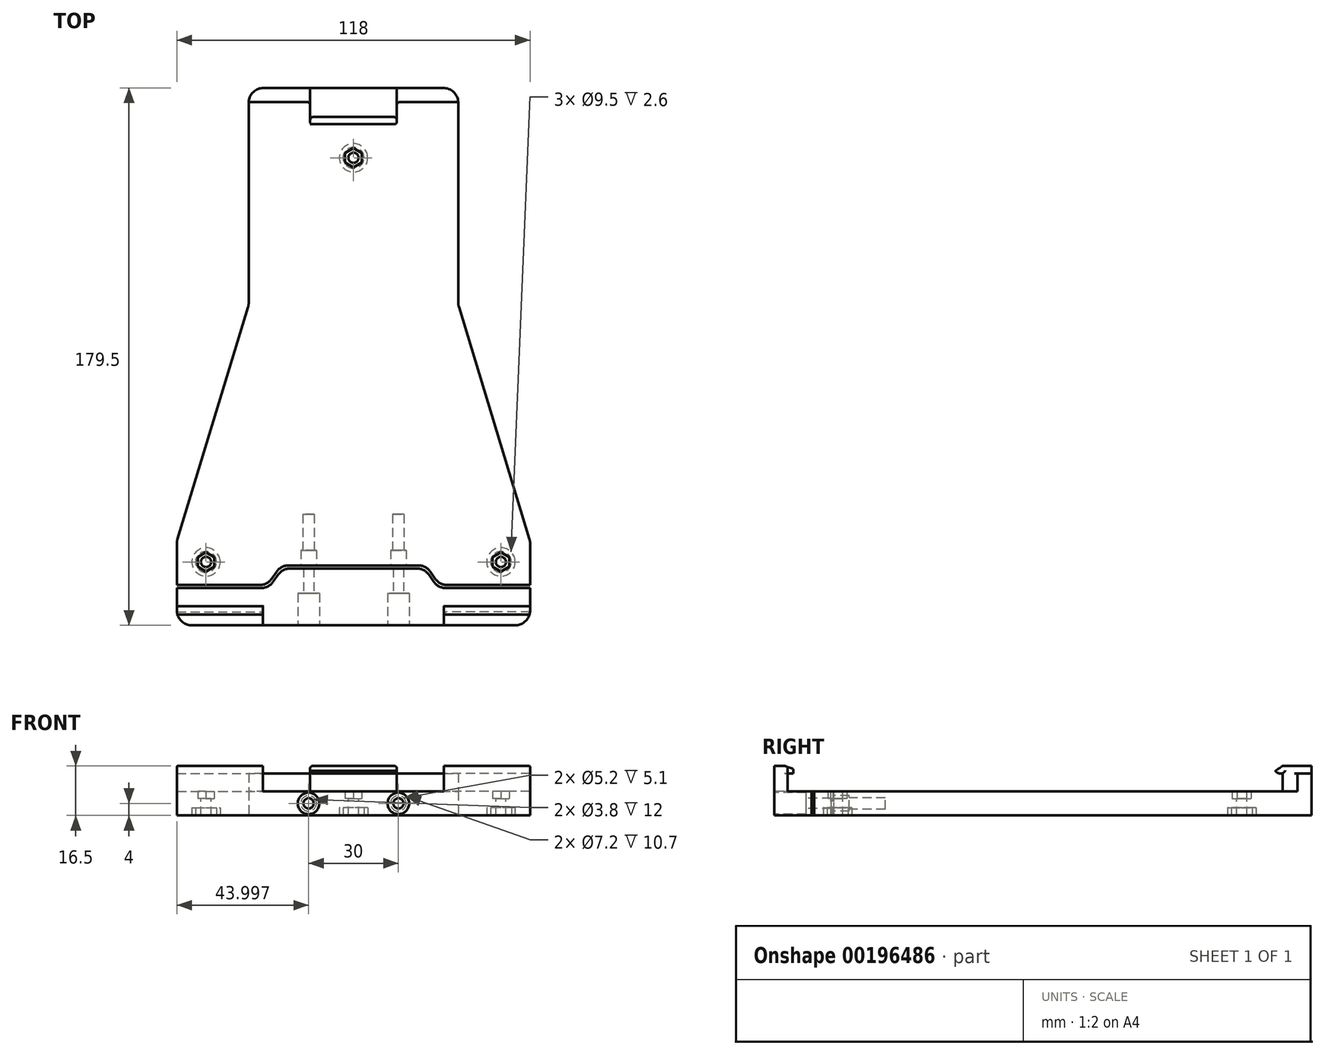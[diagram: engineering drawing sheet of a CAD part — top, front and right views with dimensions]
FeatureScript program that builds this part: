
annotation { "Feature Type Name" : "Feature", "Feature Type Description" : "" }
export const myFeature = defineFeature(function(context is Context, id is Id, definition is map)
    precondition{}
    {
        {
            var Q0;
            Q0=qCreatedBy(makeId("Top.planeOp"),FACE);
            var sketch = newSketch(context, id + "F0", { "sketchPlane" : qUnion([Q0])});
            skLineSegment(sketch, "E0.bottom", {"start": v(47.34, 124.09) * mm, "end": v(17.34, 124.09) * mm});
            skLineSegment(sketch, "E0.top", {"start": v(47.34, 51.59) * mm, "end": v(12.34, 51.59) * mm});
            skLineSegment(sketch, "E0.left", {"start": v(47.34, 124.09) * mm, "end": v(47.34, 51.59) * mm});
            skLineSegment(sketch, "E0.right", {"start": v(12.34, 119.09) * mm, "end": v(12.34, 52.33) * mm});
            skLineSegment(sketch, "E1.bottom", {"start": v(47.34, -27.41) * mm, "end": v(-11.66, -27.41) * mm});
            skLineSegment(sketch, "E1.top", {"start": v(47.34, -55.41) * mm, "end": v(-6.66, -55.41) * mm});
            skLineSegment(sketch, "E1.left", {"start": v(47.34, -27.41) * mm, "end": v(47.34, -55.41) * mm});
            skLineSegment(sketch, "E1.right", {"start": v(-11.66, -28.15) * mm, "end": v(-11.66, -50.41) * mm});
            skLineSegment(sketch, "E2", {"start": v(-11.45, -26.7) * mm, "end": v(12.12, 50.88) * mm});
            skLineSegment(sketch, "E3", {"start": v(47.34, -27.41) * mm, "end": v(47.34, 51.59) * mm});
            skCircle(sketch, "E4", {"center": v(-1.91, -34.26) * mm, "radius": 1.7 * mm});
            skCircle(sketch, "E5", {"center": v(47.34, 100.74) * mm, "radius": 1.7 * mm});
            skCircle(sketch, "E6.cCircle", {"center": v(-1.91, -34.26) * mm, "radius": 3.2 * mm, "construction": true});
            skLineSegment(sketch, "E6.0", {"start": v(-1.91, -37.46) * mm, "end": v(-4.68, -35.86) * mm});
            skLineSegment(sketch, "E6.1", {"start": v(-4.68, -35.86) * mm, "end": v(-4.68, -32.66) * mm});
            skLineSegment(sketch, "E6.2", {"start": v(-4.68, -32.66) * mm, "end": v(-1.91, -31.06) * mm});
            skLineSegment(sketch, "E6.3", {"start": v(-1.91, -31.06) * mm, "end": v(0.86, -32.66) * mm});
            skLineSegment(sketch, "E6.4", {"start": v(0.86, -32.66) * mm, "end": v(0.86, -35.86) * mm});
            skLineSegment(sketch, "E6.5", {"start": v(0.86, -35.86) * mm, "end": v(-1.91, -37.46) * mm});
            skCircle(sketch, "E7.cCircle", {"center": v(47.34, 100.74) * mm, "radius": 3.2 * mm, "construction": true});
            skLineSegment(sketch, "E7.0", {"start": v(47.34, 97.54) * mm, "end": v(44.57, 99.14) * mm});
            skLineSegment(sketch, "E7.1", {"start": v(44.57, 99.14) * mm, "end": v(44.57, 102.34) * mm});
            skLineSegment(sketch, "E7.2", {"start": v(44.57, 102.34) * mm, "end": v(47.34, 103.94) * mm});
            skLineSegment(sketch, "E7.3", {"start": v(47.34, 103.94) * mm, "end": v(50.1, 102.34) * mm});
            skLineSegment(sketch, "E7.4", {"start": v(50.1, 102.34) * mm, "end": v(50.1, 99.14) * mm});
            skLineSegment(sketch, "E7.5", {"start": v(50.1, 99.14) * mm, "end": v(47.34, 97.54) * mm});
            skPoint(sketch, "E8.visualSharp", {"position": v(-11.66, -55.41) * mm});
            skArc(sketch, "E8.filletArc", {"start": v(-11.66, -50.41) * mm, "mid": v(-10.2, -53.95) * mm, "end": v(-6.66, -55.41) * mm});
            skPoint(sketch, "E9.visualSharp", {"position": v(-11.66, -27.41) * mm});
            skArc(sketch, "E9.filletArc", {"start": v(-11.45, -26.7) * mm, "mid": v(-11.6, -27.42) * mm, "end": v(-11.66, -28.15) * mm});
            skPoint(sketch, "E10.visualSharp", {"position": v(12.34, 51.59) * mm});
            skArc(sketch, "E10.filletArc", {"start": v(12.12, 50.88) * mm, "mid": v(12.28, 51.6) * mm, "end": v(12.34, 52.33) * mm});
            skPoint(sketch, "E11.visualSharp", {"position": v(12.34, 124.09) * mm});
            skArc(sketch, "E11.filletArc", {"start": v(17.34, 124.09) * mm, "mid": v(13.8, 122.62) * mm, "end": v(12.34, 119.09) * mm});
            skLineSegment(sketch, "E12", {"start": v(0.86, -35.86) * mm, "end": v(1.25, -34.73) * mm});
            skLineSegment(sketch, "E13.MirrorCS", {"start": v(50.49, 101.3) * mm, "end": v(50.1, 102.34) * mm});
            skPoint(sketch, "E14.end.orphan", {"position": v(47.34, -37.46) * mm});
            skPoint(sketch, "E15.orphan", {"position": v(47.34, -31.06) * mm});
            skLineSegment(sketch, "E16.trimOffspring", {"start": v(44.19, 101.3) * mm, "end": v(44.57, 102.34) * mm});
            skPoint(sketch, "E17.MirrorCS.start.orphan", {"position": v(96.59, -37.46) * mm});
            skPoint(sketch, "E18.orphan", {"position": v(99.36, -32.66) * mm});
            skPoint(sketch, "E19.trimOffspring.end.orphan", {"position": v(47.34, 97.54) * mm});
            skPoint(sketch, "E20.MirrorCS.end.orphan", {"position": v(99.36, -35.86) * mm});
            skPoint(sketch, "E21.trimOffspring.start.orphan", {"position": v(93.82, -35.86) * mm});
            skPoint(sketch, "E22.MirrorCS.start.orphan", {"position": v(96.59, -31.06) * mm});
            skSolve(sketch);
        }
        {
            var Q0;
            Q0=makeQuery(id+"F0.imprint","IMPRINT",FACE,{"disambiguationData":[TD([[makeQuery(id+"F0.imprint","IMPRINT",EDGE,{"derivedFrom":sQuery(id+"F0.wireOp",EDGE,"E1.top")}),-1.0]])]});
            var Q1;
            {var subQ6=sQuery(id+"F0.wireOp",EDGE,"E0.bottom");Q1=makeQuery(id+"F0.imprint","IMPRINT",FACE,{"disambiguationData":[TD([[makeQuery(id+"F0.imprint","IMPRINT",EDGE,{"derivedFrom":subQ6}),1.0]])]});}
            extrude(context, id + "F1", {"entities" : qUnion([Q0, Q1]), "depth" : 2.4 * mm});
        }
        {
            var Q0;
            Q0=makeQuery(id+"F0.imprint","IMPRINT",FACE,{"disambiguationData":[TD([[makeQuery(id+"F0.imprint","IMPRINT",EDGE,{"derivedFrom":sQuery(id+"F0.wireOp",EDGE,"E4")}),-1.0]])]});
            var Q1;
            Q1=makeQuery(id+"F0.imprint","IMPRINT",FACE,{"disambiguationData":[TD([[makeQuery(id+"F0.imprint","IMPRINT",EDGE,{"derivedFrom":sQuery(id+"F0.wireOp",EDGE,"E1.top")}),-1.0]])]});
            var Q2;
            {var subQ4=sQuery(id+"F0.wireOp",EDGE,"E7.0");Q2=makeQuery(id+"F0.imprint","IMPRINT",FACE,{"disambiguationData":[TD([[makeQuery(id+"F0.imprint","IMPRINT",EDGE,{"derivedFrom":subQ4}),-1.0]])]});}
            var Q3;
            {var subQ6=sQuery(id+"F0.wireOp",EDGE,"E0.bottom");Q3=makeQuery(id+"F0.imprint","IMPRINT",FACE,{"disambiguationData":[TD([[makeQuery(id+"F0.imprint","IMPRINT",EDGE,{"derivedFrom":subQ6}),1.0]])]});}
            extrude(context, id + "F2", {"entities" : qUnion([Q0, Q1, Q2, Q3]), "operationType" : NewBodyOperationType.ADD, "oppositeDirection" : true, "depth" : 5.6 * mm});
        }
        {
            var Q0;
            Q0=makeQuery(id+"F2.opExtrude","CAP_FACE",FACE,{"disambiguationData":[OSD([sQuery(id+"F0.wireOp",EDGE,"E0.bottom"),sQuery(id+"F0.wireOp",EDGE,"E0.left"),sQuery(id+"F0.wireOp",EDGE,"E0.right"),sQuery(id+"F0.wireOp",EDGE,"E1.top"),sQuery(id+"F0.wireOp",EDGE,"E1.left"),sQuery(id+"F0.wireOp",EDGE,"E1.right"),sQuery(id+"F0.wireOp",EDGE,"E2"),sQuery(id+"F0.wireOp",EDGE,"E3"),sQuery(id+"F0.wireOp",EDGE,"E4"),sQuery(id+"F0.wireOp",EDGE,"E5"),sQuery(id+"F0.wireOp",EDGE,"E8.filletArc"),sQuery(id+"F0.wireOp",EDGE,"E9.filletArc"),sQuery(id+"F0.wireOp",EDGE,"E10.filletArc"),sQuery(id+"F0.wireOp",EDGE,"E11.filletArc")])],"isStart":false});
            var sketch = newSketch(context, id + "F3", { "sketchPlane" : qUnion([Q0])});
            skCircle(sketch, "E23", {"center": v(-1.91, 34.26) * mm, "radius": 3.5 * mm});
            skCircle(sketch, "E24", {"center": v(47.34, -100.74) * mm, "radius": 3.5 * mm});
            skCircle(sketch, "E25", {"center": v(-1.91, 34.26) * mm, "radius": 4.75 * mm});
            skCircle(sketch, "E26", {"center": v(47.34, -100.74) * mm, "radius": 4.75 * mm});
            skSolve(sketch);
        }
        {
            var Q0;
            {var subQ1=sQuery(id+"F0.wireOp",EDGE,"E0.left");var subQ2=makeQuery(id+"F2.opExtrude","CAP_EDGE",EDGE,{"disambiguationData":[OSD([subQ1])],"isStart":false});var subQ6=sQuery(id+"F3.wireOp",EDGE,"E26");var subQ7=makeQuery(id+"F3.imprint","INTERSECT",VERTEX,{"derivedFrom":[subQ2,subQ6]});Q0=makeQuery(id+"F3.imprint","IMPRINT",FACE,{"disambiguationData":[TD([[makeQuery(id+"F3.imprint","IMPRINT",EDGE,{"disambiguationData":[TD([[subQ7,-1.0]])],"derivedFrom":subQ2}),-1.0]])]});}
            var Q1;
            {var subQ1=sQuery(id+"F0.wireOp",EDGE,"E0.left");var subQ2=makeQuery(id+"F2.opExtrude","CAP_EDGE",EDGE,{"disambiguationData":[OSD([subQ1])],"isStart":false});var subQ6=sQuery(id+"F3.wireOp",EDGE,"E26");var subQ7=makeQuery(id+"F3.imprint","INTERSECT",VERTEX,{"derivedFrom":[subQ2,subQ6]});Q1=makeQuery(id+"F3.imprint","IMPRINT",FACE,{"disambiguationData":[TD([[makeQuery(id+"F3.imprint","IMPRINT",EDGE,{"disambiguationData":[TD([[subQ7,-1.0]])],"derivedFrom":subQ2}),1.0]])]});}
            var Q2;
            Q2=makeQuery(id+"F3.imprint","IMPRINT",FACE,{"disambiguationData":[TD([[makeQuery(id+"F3.imprint","IMPRINT",EDGE,{"derivedFrom":sQuery(id+"F3.wireOp",EDGE,"E23")}),-1.0]])]});
            extrude(context, id + "F4", {"entities" : qUnion([Q0, Q1, Q2]), "operationType" : NewBodyOperationType.REMOVE, "oppositeDirection" : true, "depth" : 2.6 * mm});
        }
        {
            var Q0;
            Q0=makeQuery(id+"F1.opExtrude","CAP_FACE",FACE,{"disambiguationData":[OSD([sQuery(id+"F0.wireOp",EDGE,"E0.bottom"),sQuery(id+"F0.wireOp",EDGE,"E0.left"),sQuery(id+"F0.wireOp",EDGE,"E0.right"),sQuery(id+"F0.wireOp",EDGE,"E1.top"),sQuery(id+"F0.wireOp",EDGE,"E1.left"),sQuery(id+"F0.wireOp",EDGE,"E1.right"),sQuery(id+"F0.wireOp",EDGE,"E2"),sQuery(id+"F0.wireOp",EDGE,"E3"),sQuery(id+"F0.wireOp",EDGE,"E6.0"),sQuery(id+"F0.wireOp",EDGE,"E6.1"),sQuery(id+"F0.wireOp",EDGE,"E6.2"),sQuery(id+"F0.wireOp",EDGE,"E6.3"),sQuery(id+"F0.wireOp",EDGE,"E6.4"),sQuery(id+"F0.wireOp",EDGE,"E6.5"),sQuery(id+"F0.wireOp",EDGE,"E7.0"),sQuery(id+"F0.wireOp",EDGE,"E7.1"),sQuery(id+"F0.wireOp",EDGE,"E7.2"),sQuery(id+"F0.wireOp",EDGE,"E8.filletArc"),sQuery(id+"F0.wireOp",EDGE,"E9.filletArc"),sQuery(id+"F0.wireOp",EDGE,"E10.filletArc"),sQuery(id+"F0.wireOp",EDGE,"E11.filletArc")])],"isStart":false});
            var sketch = newSketch(context, id + "F5", { "sketchPlane" : qUnion([Q0])});
            skLineSegment(sketch, "E27", {"start": v(-11.66, -50.98) * mm, "end": v(16.14, -50.98) * mm});
            skLineSegment(sketch, "E28", {"start": v(47.34, 114.37) * mm, "end": v(33.84, 114.37) * mm});
            skLineSegment(sketch, "E29", {"start": v(17.14, -51.98) * mm, "end": v(17.14, -55.41) * mm});
            skLineSegment(sketch, "E30", {"start": v(32.84, 115.37) * mm, "end": v(32.84, 118.37) * mm});
            skLineSegment(sketch, "E31", {"start": v(31.84, 119.37) * mm, "end": v(12.34, 119.37) * mm});
            skArc(sketch, "E32.filletArc", {"start": v(32.84, 118.37) * mm, "mid": v(32.54, 119.07) * mm, "end": v(31.84, 119.37) * mm});
            skArc(sketch, "E33.filletArc", {"start": v(32.84, 115.37) * mm, "mid": v(33.13, 114.66) * mm, "end": v(33.84, 114.37) * mm});
            skArc(sketch, "E34.filletArc", {"start": v(17.14, -51.98) * mm, "mid": v(16.84, -51.28) * mm, "end": v(16.14, -50.98) * mm});
            skSolve(sketch);
        }
        {
            var Q0;
            {var subQ3=sQuery(id+"F5.wireOp",EDGE,"E29");Q0=makeQuery(id+"F5.imprint","IMPRINT",FACE,{"disambiguationData":[TD([[makeQuery(id+"F5.imprint","IMPRINT",EDGE,{"derivedFrom":subQ3}),-1.0]])]});}
            var Q1;
            {var subQ6=sQuery(id+"F5.wireOp",EDGE,"E28");Q1=makeQuery(id+"F5.imprint","IMPRINT",FACE,{"disambiguationData":[TD([[makeQuery(id+"F5.imprint","IMPRINT",EDGE,{"derivedFrom":subQ6}),-1.0]])]});}
            extrude(context, id + "F6", {"entities" : qUnion([Q0, Q1]), "operationType" : NewBodyOperationType.ADD, "depth" : 6 * mm});
        }
        {
            var Q0;
            {var subQ0=sQuery(id+"F0.wireOp",EDGE,"E0.left");Q0=makeQuery(id+"F6.boolean.opBoolean","MERGE",FACE,{"derivedFrom":[makeQuery(id+"F2.boolean.opBoolean","MERGE",FACE,{"derivedFrom":[makeQuery(id+"F1.opExtrude","SWEPT_FACE",FACE,{"disambiguationData":[OSD([subQ0])]}),makeQuery(id+"F2.opExtrude","SWEPT_FACE",FACE,{"disambiguationData":[OSD([subQ0])]})]}),makeQuery(id+"F6.opExtrude","SWEPT_FACE",FACE,{"disambiguationData":[OSD([subQ0])]})]});}
            var sketch = newSketch(context, id + "F7", { "sketchPlane" : qUnion([Q0])});
            skLineSegment(sketch, "E35", {"start": v(114.37, 8.4) * mm, "end": v(113.61, 8.4) * mm});
            skLineSegment(sketch, "E36", {"start": v(110.77, 8.4) * mm, "end": v(114.37, 10.9) * mm});
            skLineSegment(sketch, "E37.bottom", {"start": v(114.37, 10.9) * mm, "end": v(124.09, 10.9) * mm});
            skLineSegment(sketch, "E37.top", {"start": v(114.37, 8.4) * mm, "end": v(124.09, 8.4) * mm});
            skLineSegment(sketch, "E37.left", {"start": v(114.37, 10.9) * mm, "end": v(114.37, 8.4) * mm});
            skLineSegment(sketch, "E37.right", {"start": v(124.09, 10.9) * mm, "end": v(124.09, 8.4) * mm});
            skLineSegment(sketch, "E38", {"start": v(111.98, 9.24) * mm, "end": v(111.97, 9.26) * mm});
            skPoint(sketch, "E39.newPointA", {"position": v(112.57, 8.4) * mm});
            skPoint(sketch, "E39.newPointB", {"position": v(110.77, 8.4) * mm});
            skArc(sketch, "E39.filletArc", {"start": v(111.97, 9.26) * mm, "mid": v(112.69, 8.63) * mm, "end": v(113.61, 8.4) * mm});
            skSolve(sketch);
        }
        {
            var Q0;
            Q0 = qSketchRegion(id + "F7", true);
            extrude(context, id + "F8", {"entities" : qUnion([Q0]), "operationType" : NewBodyOperationType.ADD, "oppositeDirection" : true, "depth" : 14.5 * mm});
        }
        {
            var Q0;
            {var subQ2=sQuery(id+"F0.wireOp",EDGE,"E0.bottom");var subQ4=sQuery(id+"F7.wireOp",EDGE,"E37.top");var subQ5=sQuery(id+"F7.wireOp",EDGE,"E35");Q0=makeQuery(id+"F8.boolean.opBoolean","SPLIT",EDGE,{"disambiguationData":[TD([makeQuery(id+"F1.opExtrude","SWEPT_FACE",FACE,{"disambiguationData":[OSD([subQ2])]})])],"derivedFrom":makeQuery(id+"F8.opExtrude","CAP_EDGE",EDGE,{"disambiguationData":[OSD([subQ5,subQ4])],"isStart":false})});}
            var Q1;
            Q1=makeQuery(id+"F8.opExtrude","CAP_EDGE",EDGE,{"disambiguationData":[OSD([sQuery(id+"F7.wireOp",EDGE,"E37.bottom")])],"isStart":false});
            fillet(context, id + "F9", {"entities" : qUnion([Q0, Q1]), "radius" : 1 * mm, "tangentPropagation" : true, "rho" : 0.5, "crossSection" : FilletCrossSection.CONIC, "allowEdgeOverflow" : false});
        }
        {
            var Q0;
            Q0=makeQuery(id+"F6.opExtrude","SWEPT_FACE",FACE,{"disambiguationData":[OSD([sQuery(id+"F5.wireOp",EDGE,"E29")])]});
            var sketch = newSketch(context, id + "F10", { "sketchPlane" : qUnion([Q0])});
            skLineSegment(sketch, "E40", {"start": v(-55.41, 8.4) * mm, "end": v(-49.01, 8.4) * mm});
            skLineSegment(sketch, "E41", {"start": v(-55.41, 8.4) * mm, "end": v(-55.41, 10.9) * mm});
            skLineSegment(sketch, "E42", {"start": v(-55.41, 10.9) * mm, "end": v(-51.81, 10.9) * mm});
            skLineSegment(sketch, "E43", {"start": v(-55.41, 8.4) * mm, "end": v(-51.81, 8.4) * mm});
            skLineSegment(sketch, "E44", {"start": v(-49.01, 8.4) * mm, "end": v(-49.01, 9.55) * mm});
            skLineSegment(sketch, "E45", {"start": v(-49.34, 10.02) * mm, "end": v(-51.81, 10.9) * mm});
            skPoint(sketch, "E46.start.orphan", {"position": v(-50.41, 9.65) * mm});
            skPoint(sketch, "E47.visualSharp", {"position": v(-49.01, 9.9) * mm});
            skArc(sketch, "E47.filletArc", {"start": v(-49.01, 9.55) * mm, "mid": v(-49.1, 9.84) * mm, "end": v(-49.34, 10.02) * mm});
            skSolve(sketch);
        }
        {
            var Q0;
            {var subQ0=sQuery(id+"F10.wireOp",EDGE,"E41");Q0=makeQuery(id+"F10.imprint","IMPRINT",FACE,{"disambiguationData":[TD([[makeQuery(id+"F10.imprint","IMPRINT",EDGE,{"derivedFrom":subQ0}),-1.0]])]});}
            extrude(context, id + "F11", {"entities" : qUnion([Q0]), "operationType" : NewBodyOperationType.ADD, "oppositeDirection" : true, "depth" : 28.77 * mm});
        }
        {
            var Q0;
            {var subQ1=sQuery(id+"F0.wireOp",EDGE,"E1.top");var subQ3=sQuery(id+"F10.wireOp",EDGE,"E40");Q0=makeQuery(id+"F11.boolean.opBoolean","SPLIT",FACE,{"disambiguationData":[TD([makeQuery(id+"F1.opExtrude","SWEPT_FACE",FACE,{"disambiguationData":[OSD([subQ1])]})])],"derivedFrom":makeQuery(id+"F11.opExtrude","SWEPT_FACE",FACE,{"disambiguationData":[OSD([subQ3])]})});}
            extrude(context, id + "F12", {"entities" : qUnion([Q0]), "operationType" : NewBodyOperationType.REMOVE, "endBound" : BoundingType.UP_TO_NEXT, "oppositeDirection" : true, "depth" : 25 * mm});
        }
        {
            var Q0;
            Q0=makeQuery(id+"F1.opExtrude","CAP_FACE",FACE,{"disambiguationData":[OSD([sQuery(id+"F0.wireOp",EDGE,"E0.bottom"),sQuery(id+"F0.wireOp",EDGE,"E0.left"),sQuery(id+"F0.wireOp",EDGE,"E0.right"),sQuery(id+"F0.wireOp",EDGE,"E1.top"),sQuery(id+"F0.wireOp",EDGE,"E1.left"),sQuery(id+"F0.wireOp",EDGE,"E1.right"),sQuery(id+"F0.wireOp",EDGE,"E2"),sQuery(id+"F0.wireOp",EDGE,"E3"),sQuery(id+"F0.wireOp",EDGE,"E6.0"),sQuery(id+"F0.wireOp",EDGE,"E6.1"),sQuery(id+"F0.wireOp",EDGE,"E6.2"),sQuery(id+"F0.wireOp",EDGE,"E6.3"),sQuery(id+"F0.wireOp",EDGE,"E6.4"),sQuery(id+"F0.wireOp",EDGE,"E6.5"),sQuery(id+"F0.wireOp",EDGE,"E7.0"),sQuery(id+"F0.wireOp",EDGE,"E7.1"),sQuery(id+"F0.wireOp",EDGE,"E7.2"),sQuery(id+"F0.wireOp",EDGE,"E8.filletArc"),sQuery(id+"F0.wireOp",EDGE,"E9.filletArc"),sQuery(id+"F0.wireOp",EDGE,"E10.filletArc"),sQuery(id+"F0.wireOp",EDGE,"E11.filletArc")])],"isStart":false});
            var sketch = newSketch(context, id + "F13", { "sketchPlane" : qUnion([Q0])});
            skLineSegment(sketch, "E48", {"start": v(-11.66, -42.98) * mm, "end": v(16.45, -42.98) * mm});
            skLineSegment(sketch, "E49", {"start": v(-11.66, -41.98) * mm, "end": v(15.93, -41.98) * mm});
            skLineSegment(sketch, "E50", {"start": v(20.03, -39.84) * mm, "end": v(21.63, -37.55) * mm});
            skLineSegment(sketch, "E51", {"start": v(25.73, -35.41) * mm, "end": v(47.34, -35.41) * mm});
            skLineSegment(sketch, "E52", {"start": v(21.25, -38.1) * mm, "end": v(22.07, -38.67) * mm});
            skLineSegment(sketch, "E53", {"start": v(22.07, -38.67) * mm, "end": v(20.55, -40.84) * mm});
            skLineSegment(sketch, "E54", {"start": v(22.07, -38.67) * mm, "end": v(22.15, -38.55) * mm});
            skLineSegment(sketch, "E55", {"start": v(47.34, -36.41) * mm, "end": v(26.25, -36.41) * mm});
            skArc(sketch, "E56.filletArc", {"start": v(26.25, -36.41) * mm, "mid": v(23.94, -36.98) * mm, "end": v(22.15, -38.55) * mm});
            skPoint(sketch, "E57.visualSharp", {"position": v(23.12, -35.41) * mm});
            skArc(sketch, "E57.filletArc", {"start": v(25.73, -35.41) * mm, "mid": v(23.42, -35.98) * mm, "end": v(21.63, -37.55) * mm});
            skPoint(sketch, "E58.newPointA", {"position": v(17.84, -42.98) * mm});
            skArc(sketch, "E58.filletArc", {"start": v(15.93, -41.98) * mm, "mid": v(18.24, -41.42) * mm, "end": v(20.03, -39.84) * mm});
            skPoint(sketch, "E59.newPointA", {"position": v(47.34, -42.98) * mm});
            skArc(sketch, "E59.filletArc", {"start": v(16.45, -42.98) * mm, "mid": v(18.76, -42.42) * mm, "end": v(20.55, -40.84) * mm});
            skSolve(sketch);
        }
        {
            var Q0;
            {var subQ4=sQuery(id+"F13.wireOp",EDGE,"E48");Q0=makeQuery(id+"F13.imprint","IMPRINT",FACE,{"disambiguationData":[TD([[makeQuery(id+"F13.imprint","IMPRINT",EDGE,{"derivedFrom":subQ4}),1.0]])]});}
            var Q1;
            {var subQ1=sQuery(id+"F13.wireOp",EDGE,"E51");Q1=makeQuery(id+"F13.imprint","IMPRINT",FACE,{"disambiguationData":[TD([[makeQuery(id+"F13.imprint","IMPRINT",EDGE,{"derivedFrom":subQ1}),-1.0]])]});}
            extrude(context, id + "F14", {"entities" : qUnion([Q0, Q1]), "operationType" : NewBodyOperationType.REMOVE, "endBound" : BoundingType.THROUGH_ALL, "oppositeDirection" : true, "depth" : 25 * mm});
        }
        {
            var Q0;
            {var subQ0=sQuery(id+"F0.wireOp",EDGE,"E1.top");Q0=makeQuery(id+"F11.boolean.opBoolean","MERGE",FACE,{"derivedFrom":[makeQuery(id+"F6.boolean.opBoolean","MERGE",FACE,{"derivedFrom":[makeQuery(id+"F2.boolean.opBoolean","MERGE",FACE,{"derivedFrom":[makeQuery(id+"F1.opExtrude","SWEPT_FACE",FACE,{"disambiguationData":[OSD([subQ0])]}),makeQuery(id+"F2.opExtrude","SWEPT_FACE",FACE,{"disambiguationData":[OSD([subQ0])]})]}),makeQuery(id+"F6.opExtrude","SWEPT_FACE",FACE,{"disambiguationData":[OSD([subQ0])]})]}),makeQuery(id+"F11.opExtrude","SWEPT_FACE",FACE,{"disambiguationData":[OSD([sQuery(id+"F10.wireOp",EDGE,"E41")])]})]});}
            var sketch = newSketch(context, id + "F15", { "sketchPlane" : qUnion([Q0])});
            skCircle(sketch, "E60", {"center": v(32.34, -1.6) * mm, "radius": 3.6 * mm});
            skSolve(sketch);
        }
        {
            var Q0;
            Q0=makeQuery(id+"F15.imprint","IMPRINT",FACE,{"disambiguationData":[TD([[makeQuery(id+"F15.imprint","IMPRINT",EDGE,{"derivedFrom":sQuery(id+"F15.wireOp",EDGE,"E60")}),1.0]])]});
            extrude(context, id + "F16", {"entities" : qUnion([Q0]), "operationType" : NewBodyOperationType.REMOVE, "oppositeDirection" : true, "depth" : 10.7 * mm});
        }
        {
            var Q0;
            Q0=makeQuery(id+"F16.boolean.opBoolean","COPY",FACE,{"derivedFrom":makeQuery(id+"F16.opExtrude","CAP_FACE",FACE,{"disambiguationData":[OSD([sQuery(id+"F15.wireOp",EDGE,"E60")])],"isStart":false})});
            var sketch = newSketch(context, id + "F17", { "sketchPlane" : qUnion([Q0])});
            skCircle(sketch, "E61", {"center": v(32.34, -1.6) * mm, "radius": 1.7 * mm});
            skSolve(sketch);
        }
        {
            var Q0;
            Q0=makeQuery(id+"F17.imprint","IMPRINT",FACE,{"disambiguationData":[TD([[makeQuery(id+"F17.imprint","IMPRINT",EDGE,{"derivedFrom":sQuery(id+"F17.wireOp",EDGE,"E61")}),1.0]])]});
            extrude(context, id + "F18", {"entities" : qUnion([Q0]), "operationType" : NewBodyOperationType.REMOVE, "endBound" : BoundingType.UP_TO_NEXT, "oppositeDirection" : true, "depth" : 25 * mm});
        }
        {
            var Q0;
            Q0=makeQuery(id+"F14.boolean.opBoolean","COPY",FACE,{"derivedFrom":makeQuery(id+"F14.opExtrude","SWEPT_FACE",FACE,{"disambiguationData":[OSD([sQuery(id+"F13.wireOp",EDGE,"E51")])]})});
            var sketch = newSketch(context, id + "F19", { "sketchPlane" : qUnion([Q0])});
            skCircle(sketch, "E62.0", {"center": v(32.34, -1.6) * mm, "radius": 3.6 * mm});
            skCircle(sketch, "E63", {"center": v(32.34, -1.6) * mm, "radius": 2.6 * mm});
            skSolve(sketch);
        }
        {
            var Q0;
            Q0=makeQuery(id+"F19.imprint","IMPRINT",FACE,{"disambiguationData":[TD([[makeQuery(id+"F19.imprint","IMPRINT",EDGE,{"derivedFrom":sQuery(id+"F19.wireOp",EDGE,"E63")}),1.0]])]});
            extrude(context, id + "F20", {"entities" : qUnion([Q0]), "operationType" : NewBodyOperationType.REMOVE, "oppositeDirection" : true, "depth" : 5.1 * mm});
        }
        {
            var Q0;
            Q0=makeQuery(id+"F20.boolean.opBoolean","COPY",FACE,{"derivedFrom":makeQuery(id+"F20.opExtrude","CAP_FACE",FACE,{"disambiguationData":[OSD([sQuery(id+"F19.wireOp",EDGE,"E63")])],"isStart":false})});
            var sketch = newSketch(context, id + "F21", { "sketchPlane" : qUnion([Q0])});
            skCircle(sketch, "E64", {"center": v(32.34, -1.6) * mm, "radius": 1.9 * mm});
            skSolve(sketch);
        }
        {
            var Q0;
            Q0 = qSketchRegion(id + "F21", true);
            extrude(context, id + "F22", {"entities" : qUnion([Q0]), "operationType" : NewBodyOperationType.REMOVE, "oppositeDirection" : true, "depth" : 12 * mm});
        }
        {
            var Q0;
            Q0=makeQuery(id+"F14.boolean.opBoolean","SPLIT",BODY,{"disambiguationData":[OD(0.0)],"derivedFrom":makeQuery(id+"F1.opExtrude","SWEPT_BODY",BODY,{"disambiguationData":[OSD([sQuery(id+"F0.wireOp",EDGE,"E0.bottom"),sQuery(id+"F0.wireOp",EDGE,"E0.left"),sQuery(id+"F0.wireOp",EDGE,"E0.right"),sQuery(id+"F0.wireOp",EDGE,"E1.top"),sQuery(id+"F0.wireOp",EDGE,"E1.left"),sQuery(id+"F0.wireOp",EDGE,"E1.right"),sQuery(id+"F0.wireOp",EDGE,"E2"),sQuery(id+"F0.wireOp",EDGE,"E3"),sQuery(id+"F0.wireOp",EDGE,"E6.0"),sQuery(id+"F0.wireOp",EDGE,"E6.1"),sQuery(id+"F0.wireOp",EDGE,"E6.2"),sQuery(id+"F0.wireOp",EDGE,"E6.3"),sQuery(id+"F0.wireOp",EDGE,"E6.4"),sQuery(id+"F0.wireOp",EDGE,"E6.5"),sQuery(id+"F0.wireOp",EDGE,"E7.0"),sQuery(id+"F0.wireOp",EDGE,"E7.1"),sQuery(id+"F0.wireOp",EDGE,"E7.2"),sQuery(id+"F0.wireOp",EDGE,"E8.filletArc"),sQuery(id+"F0.wireOp",EDGE,"E9.filletArc"),sQuery(id+"F0.wireOp",EDGE,"E10.filletArc"),sQuery(id+"F0.wireOp",EDGE,"E11.filletArc")])]})});
            var Q1;
            {var subQ6=sQuery(id+"F0.wireOp",EDGE,"E3");var subQ9=sQuery(id+"F0.wireOp",EDGE,"E1.left");var subQ12=sQuery(id+"F0.wireOp",EDGE,"E0.left");var subQ15=sQuery(id+"F0.wireOp",EDGE,"E7.0");Q1=makeQuery(id+"F14.boolean.opBoolean","SPLIT",FACE,{"disambiguationData":[TD([makeQuery(id+"F1.opExtrude","SWEPT_FACE",FACE,{"disambiguationData":[OSD([subQ15])]})])],"derivedFrom":makeQuery(id+"F2.boolean.opBoolean","MERGE",FACE,{"derivedFrom":[makeQuery(id+"F1.opExtrude","SWEPT_FACE",FACE,{"disambiguationData":[OSD([subQ12,subQ9,subQ6])]}),makeQuery(id+"F2.opExtrude","SWEPT_FACE",FACE,{"disambiguationData":[OSD([subQ12,subQ9,subQ6])]})]})});}
            mirror(context, id + "F23", {"operationType" : NewBodyOperationType.ADD, "entities" : qUnion([Q0]), "mirrorPlane" : qUnion([Q1])});
        }
        {
            var Q0;
            Q0=makeQuery(id+"F14.boolean.opBoolean","SPLIT",BODY,{"disambiguationData":[OD(1.0)],"derivedFrom":makeQuery(id+"F1.opExtrude","SWEPT_BODY",BODY,{"disambiguationData":[OSD([sQuery(id+"F0.wireOp",EDGE,"E0.bottom"),sQuery(id+"F0.wireOp",EDGE,"E0.left"),sQuery(id+"F0.wireOp",EDGE,"E0.right"),sQuery(id+"F0.wireOp",EDGE,"E1.top"),sQuery(id+"F0.wireOp",EDGE,"E1.left"),sQuery(id+"F0.wireOp",EDGE,"E1.right"),sQuery(id+"F0.wireOp",EDGE,"E2"),sQuery(id+"F0.wireOp",EDGE,"E3"),sQuery(id+"F0.wireOp",EDGE,"E6.0"),sQuery(id+"F0.wireOp",EDGE,"E6.1"),sQuery(id+"F0.wireOp",EDGE,"E6.2"),sQuery(id+"F0.wireOp",EDGE,"E6.3"),sQuery(id+"F0.wireOp",EDGE,"E6.4"),sQuery(id+"F0.wireOp",EDGE,"E6.5"),sQuery(id+"F0.wireOp",EDGE,"E7.0"),sQuery(id+"F0.wireOp",EDGE,"E7.1"),sQuery(id+"F0.wireOp",EDGE,"E7.2"),sQuery(id+"F0.wireOp",EDGE,"E8.filletArc"),sQuery(id+"F0.wireOp",EDGE,"E9.filletArc"),sQuery(id+"F0.wireOp",EDGE,"E10.filletArc"),sQuery(id+"F0.wireOp",EDGE,"E11.filletArc")])]})});
            var Q1;
            {var subQ4=sQuery(id+"F0.wireOp",EDGE,"E3");var subQ7=sQuery(id+"F0.wireOp",EDGE,"E1.left");var subQ8=sQuery(id+"F0.wireOp",EDGE,"E1.top");var subQ10=sQuery(id+"F0.wireOp",EDGE,"E0.left");Q1=makeQuery(id+"F14.boolean.opBoolean","SPLIT",FACE,{"disambiguationData":[TD([makeQuery(id+"F1.opExtrude","SWEPT_FACE",FACE,{"disambiguationData":[OSD([subQ8])]})])],"derivedFrom":makeQuery(id+"F2.boolean.opBoolean","MERGE",FACE,{"derivedFrom":[makeQuery(id+"F1.opExtrude","SWEPT_FACE",FACE,{"disambiguationData":[OSD([subQ10,subQ7,subQ4])]}),makeQuery(id+"F2.opExtrude","SWEPT_FACE",FACE,{"disambiguationData":[OSD([subQ10,subQ7,subQ4])]})]})});}
            mirror(context, id + "F24", {"operationType" : NewBodyOperationType.ADD, "entities" : qUnion([Q0]), "mirrorPlane" : qUnion([Q1])});
        }
    });
